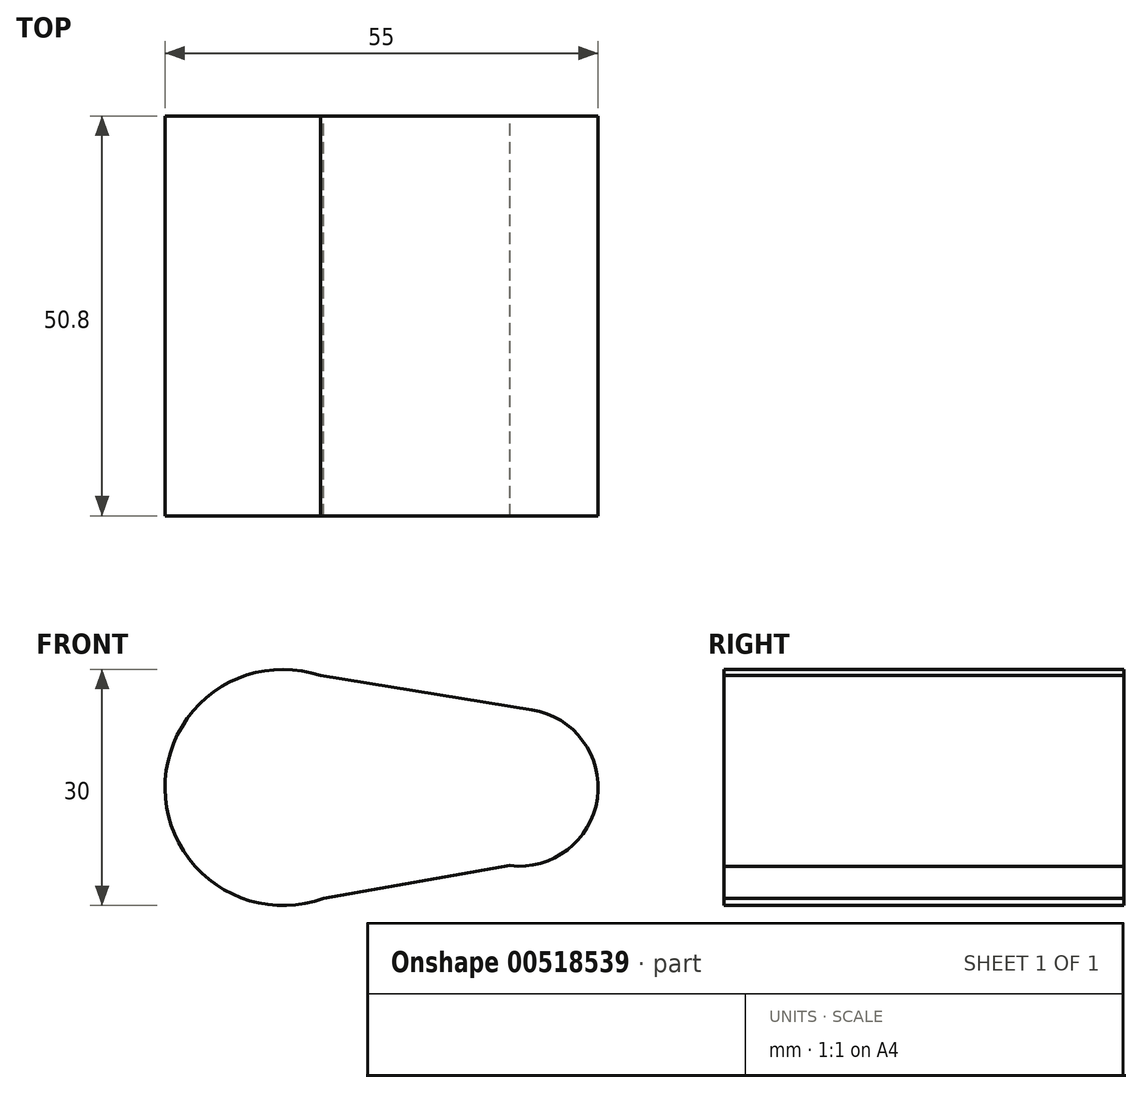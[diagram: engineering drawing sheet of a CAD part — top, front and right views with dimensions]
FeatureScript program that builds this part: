
annotation { "Feature Type Name" : "Feature", "Feature Type Description" : "" }
export const myFeature = defineFeature(function(context is Context, id is Id, definition is map)
    precondition{}
    {
        {
            var Q0;
            Q0=qCreatedBy(makeId("Front.planeOp"),FACE);
            var sketch = newSketch(context, id + "F0", { "sketchPlane" : qUnion([Q0])});
            skCircle(sketch, "E0", {"center": v(0, 0) * mm, "radius": 15 * mm});
            skCircle(sketch, "E1", {"center": v(30, 0) * mm, "radius": 10 * mm});
            skLineSegment(sketch, "E2", {"start": v(0, 15) * mm, "end": v(31.6, 9.87) * mm});
            skLineSegment(sketch, "E3", {"start": v(0, -15) * mm, "end": v(28.8, -9.93) * mm});
            skArc(sketch, "E4", {"start": v(31.6, 9.87) * mm, "mid": v(34.07, 9.13) * mm, "end": v(36.27, 7.8) * mm});
            skSolve(sketch);
        }
        {
            var Q0;
            Q0 = qSketchRegion(id + "F0", true);
            extrude(context, id + "F1", {"entities" : qUnion([Q0]), "depth" : 50.8 * mm, "offsetDistance" : 25.4 * mm});
        }
    });
